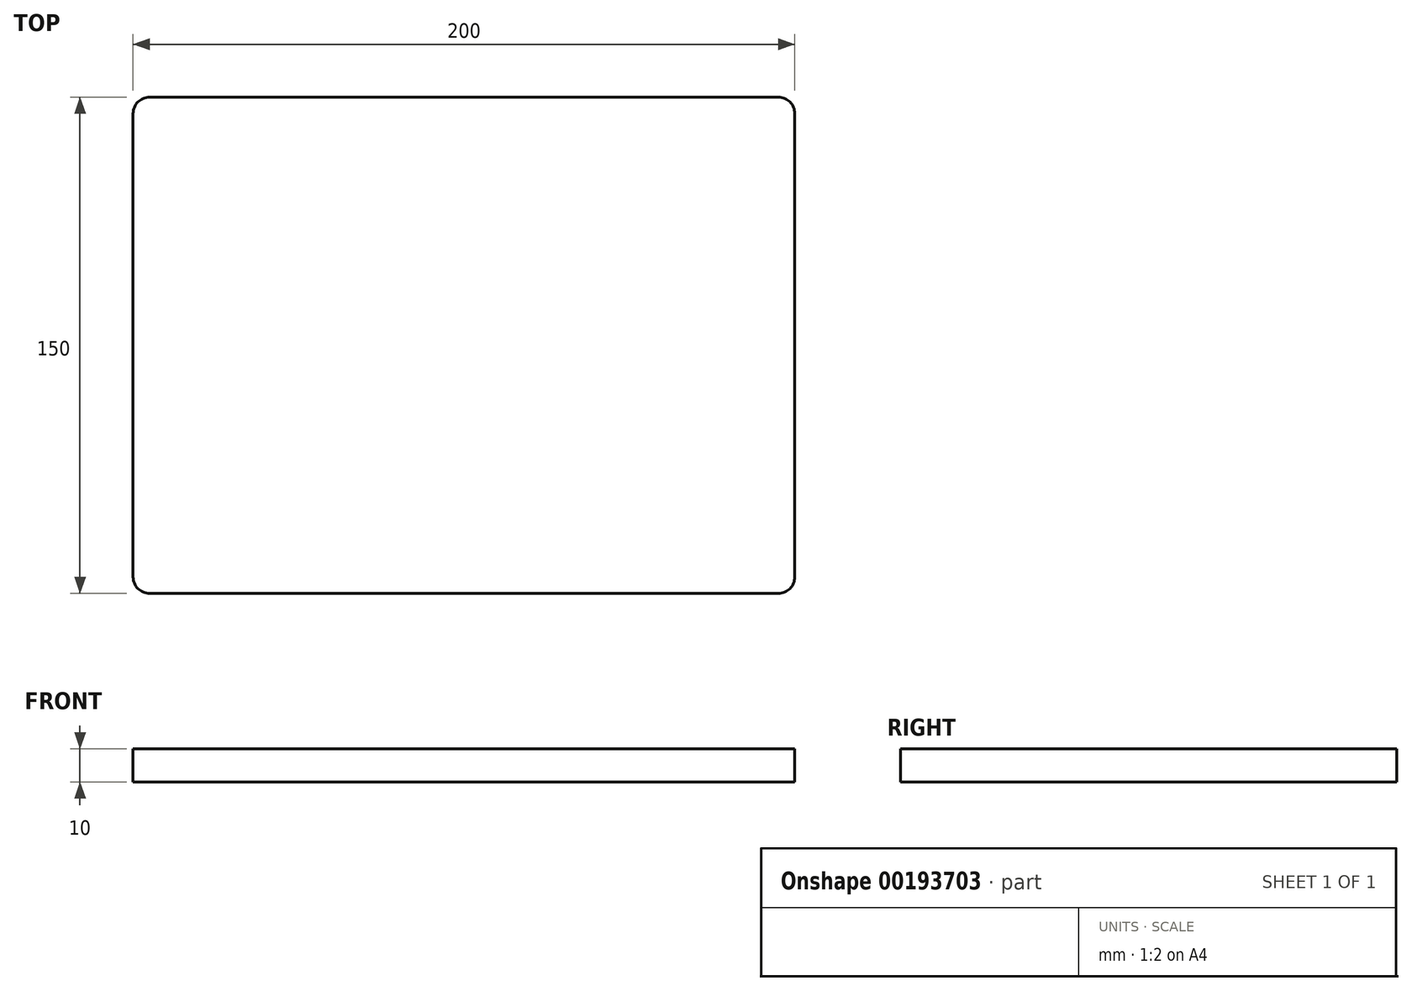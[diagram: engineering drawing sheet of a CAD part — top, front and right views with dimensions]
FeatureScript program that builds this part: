
annotation { "Feature Type Name" : "Feature", "Feature Type Description" : "" }
export const myFeature = defineFeature(function(context is Context, id is Id, definition is map)
    precondition{}
    {
        {
            var Q0;
            Q0=qCreatedBy(makeId("Top.planeOp"),FACE);
            var sketch = newSketch(context, id + "F0", { "sketchPlane" : qUnion([Q0])});
            skLineSegment(sketch, "E0.bottom", {"start": v(-98.9, 83.02) * mm, "end": v(101.1, 83.02) * mm});
            skLineSegment(sketch, "E0.top", {"start": v(-98.9, -66.98) * mm, "end": v(101.1, -66.98) * mm});
            skLineSegment(sketch, "E0.left", {"start": v(-98.9, 83.02) * mm, "end": v(-98.9, -66.98) * mm});
            skLineSegment(sketch, "E0.right", {"start": v(101.1, 83.02) * mm, "end": v(101.1, -66.98) * mm});
            skSolve(sketch);
        }
        {
            var Q0;
            Q0=makeQuery(id+"F0.imprint","IMPRINT",FACE,{"disambiguationData":[TD([[makeQuery(id+"F0.imprint","IMPRINT",EDGE,{"derivedFrom":sQuery(id+"F0.wireOp",EDGE,"E0.bottom")}),-1.0]])]});
            extrude(context, id + "F1", {"entities" : qUnion([Q0]), "depth" : 5 * mm});
        }
        {
            var Q0;
            Q0=makeQuery(id+"F1.opExtrude","SWEPT_EDGE",EDGE,{"disambiguationData":[OSD([sQuery(id+"F0.wireOp",EDGE,"E0.top"),sQuery(id+"F0.wireOp",EDGE,"E0.left")])]});
            fillet(context, id + "F2", {"entities" : qUnion([Q0]), "radius" : 5 * mm, "tangentPropagation" : true, "allowEdgeOverflow" : false});
        }
        {
            var Q0;
            Q0=makeQuery(id+"F1.opExtrude","SWEPT_EDGE",EDGE,{"disambiguationData":[OSD([sQuery(id+"F0.wireOp",EDGE,"E0.bottom"),sQuery(id+"F0.wireOp",EDGE,"E0.left")])]});
            fillet(context, id + "F3", {"entities" : qUnion([Q0]), "radius" : 5 * mm, "tangentPropagation" : true, "allowEdgeOverflow" : false});
        }
        {
            var Q0;
            Q0=makeQuery(id+"F1.opExtrude","SWEPT_EDGE",EDGE,{"disambiguationData":[OSD([sQuery(id+"F0.wireOp",EDGE,"E0.top"),sQuery(id+"F0.wireOp",EDGE,"E0.right")])]});
            fillet(context, id + "F4", {"entities" : qUnion([Q0]), "radius" : 5 * mm, "tangentPropagation" : true, "allowEdgeOverflow" : false});
        }
        {
            var Q0;
            Q0=makeQuery(id+"F1.opExtrude","SWEPT_EDGE",EDGE,{"disambiguationData":[OSD([sQuery(id+"F0.wireOp",EDGE,"E0.bottom"),sQuery(id+"F0.wireOp",EDGE,"E0.right")])]});
            fillet(context, id + "F5", {"entities" : qUnion([Q0]), "radius" : 5 * mm, "tangentPropagation" : true, "allowEdgeOverflow" : false});
        }
        {
            var Q0;
            Q0=makeQuery(id+"F1.opExtrude","CAP_FACE",FACE,{"disambiguationData":[OSD([sQuery(id+"F0.wireOp",EDGE,"E0.bottom"),sQuery(id+"F0.wireOp",EDGE,"E0.top"),sQuery(id+"F0.wireOp",EDGE,"E0.left"),sQuery(id+"F0.wireOp",EDGE,"E0.right")])],"isStart":false});
            var sketch = newSketch(context, id + "F6", { "sketchPlane" : qUnion([Q0])});
            skCircle(sketch, "E1", {"center": v(46.03, -36.82) * mm, "radius": 1.5 * mm});
            skCircle(sketch, "E2", {"center": v(16.45, -38.03) * mm, "radius": 1.5 * mm});
            skCircle(sketch, "E3.MirrorC", {"center": v(-46.03, -36.82) * mm, "radius": 1.5 * mm});
            skCircle(sketch, "E4.MirrorC", {"center": v(-16.45, -38.03) * mm, "radius": 1.5 * mm});
            skCircle(sketch, "E5.MirrorC", {"center": v(46.03, 36.82) * mm, "radius": 1.5 * mm});
            skSolve(sketch);
        }
        {
            var Q0;
            Q0=makeQuery(id+"F1.opExtrude","SWEPT_BODY",BODY,{"disambiguationData":[OSD([sQuery(id+"F0.wireOp",EDGE,"E0.bottom"),sQuery(id+"F0.wireOp",EDGE,"E0.top"),sQuery(id+"F0.wireOp",EDGE,"E0.left"),sQuery(id+"F0.wireOp",EDGE,"E0.right")])]});
            var Q1;
            Q1=makeQuery(id+"F6.imprint","IMPRINT",FACE,{"disambiguationData":[TD([[makeQuery(id+"F6.imprint","IMPRINT",EDGE,{"derivedFrom":sQuery(id+"F6.wireOp",EDGE,"E3.MirrorC")}),1.0]])]});
            mirror(context, id + "F7", {"operationType" : NewBodyOperationType.ADD, "entities" : qUnion([Q0]), "mirrorPlane" : qUnion([Q1])});
        }
    });
